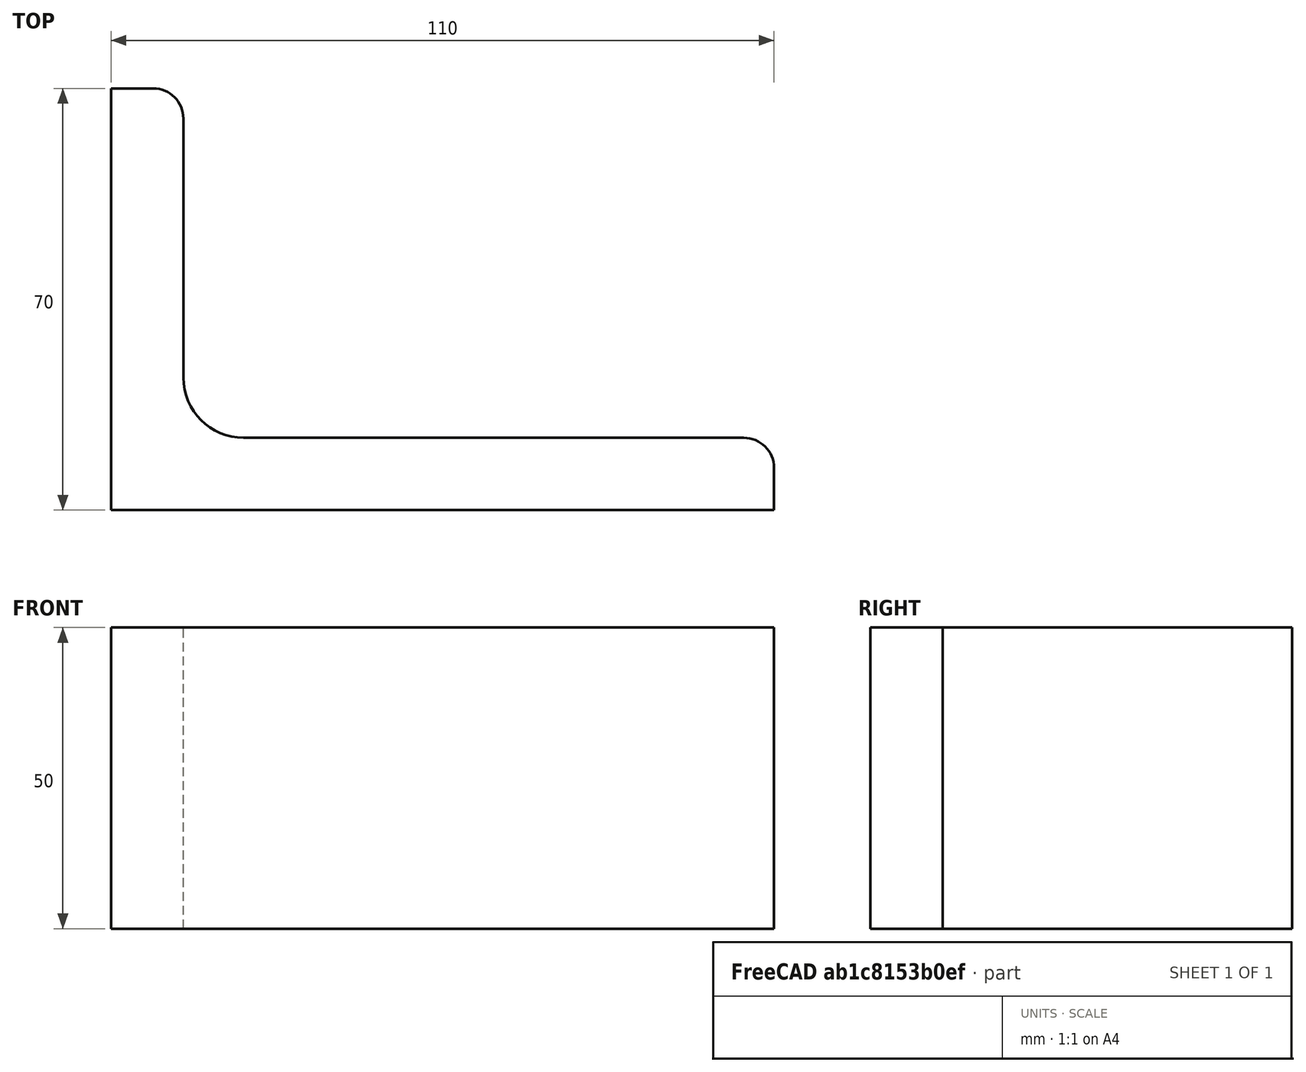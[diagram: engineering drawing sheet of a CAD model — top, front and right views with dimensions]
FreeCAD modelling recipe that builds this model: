
FCSTD DOCUMENT  (FreeCAD 0.15R4671 (Git))
Label: Angle Bar 110x70x12 EN10056 S235JR
License: All rights reserved
LicenseURL: http://en.wikipedia.org/wiki/All_rights_reserved
objects: Sketcher::SketchObject×1, Part::Extrusion×1
note: 2 computed .brp shape members not serialized (recipe doc carries the construction recipe); baked Part::Feature solids carry a one-line shape summary decoded from their .brp

FEATURE [Sketcher::SketchObject] Sketch
  sketch-geometry (9):
    g0: LineSegment StartX=0 StartY=0 StartZ=0 EndX=110 EndY=0 EndZ=0
    g1: LineSegment StartX=110 StartY=0 StartZ=0 EndX=110 EndY=7 EndZ=0
    g2: LineSegment StartX=105 StartY=12 StartZ=0 EndX=22 EndY=12 EndZ=0
    g3: LineSegment StartX=0 StartY=0 StartZ=0 EndX=0 EndY=70 EndZ=0
    g4: LineSegment StartX=0 StartY=70 StartZ=0 EndX=7 EndY=70 EndZ=0
    g5: LineSegment StartX=12 StartY=65 StartZ=0 EndX=12 EndY=22 EndZ=0
    g6: ArcOfCircle CenterX=22 CenterY=22 CenterZ=0 NormalX=0 NormalY=0 NormalZ=1 Radius=10 StartAngle=3.14159 EndAngle=4.71239
    g7: ArcOfCircle CenterX=7 CenterY=65 CenterZ=0 NormalX=0 NormalY=0 NormalZ=1 Radius=5 StartAngle=0 EndAngle=1.5708
    g8: ArcOfCircle CenterX=105 CenterY=7 CenterZ=0 NormalX=0 NormalY=0 NormalZ=1 Radius=5 StartAngle=0 EndAngle=1.5708
  constraints (23):
    c: Coincident(g0,g-1)
    c: Horizontal(g0)
    c: Coincident(g1,g0)
    c: Vertical(g1)
    c: Horizontal(g2)
    c: Coincident(g3,g-1)
    c: Vertical(g3)
    c: Coincident(g4,g3)
    c: Horizontal(g4)
    c: Vertical(g5)
    c: Tangent(g5,g6) = -1.5708
    c: Tangent(g2,g6) = 1.5708
    c: Tangent(g4,g7) = 1.5708
    c: Tangent(g5,g7) = 1.5708
    c: Tangent(g2,g8) = -1.5708
    c: Tangent(g1,g8) = -1.5708
    c: DistanceX(g0) = 110
    c: DistanceY(g3) = 70
    c: DistanceY(g0,g2) = 12
    c: DistanceX(g3,g5) = 12
    c: Radius(g6) = 10
    c: Radius(g8) = 5
    c: Radius(g7) = 5
FEATURE [Part::Extrusion] Extrude  label="Angle Bar 110x70x12 EN10056 S235JR"
  Base = -> Sketch
  Dir = (0,0,50)
  Solid = true
